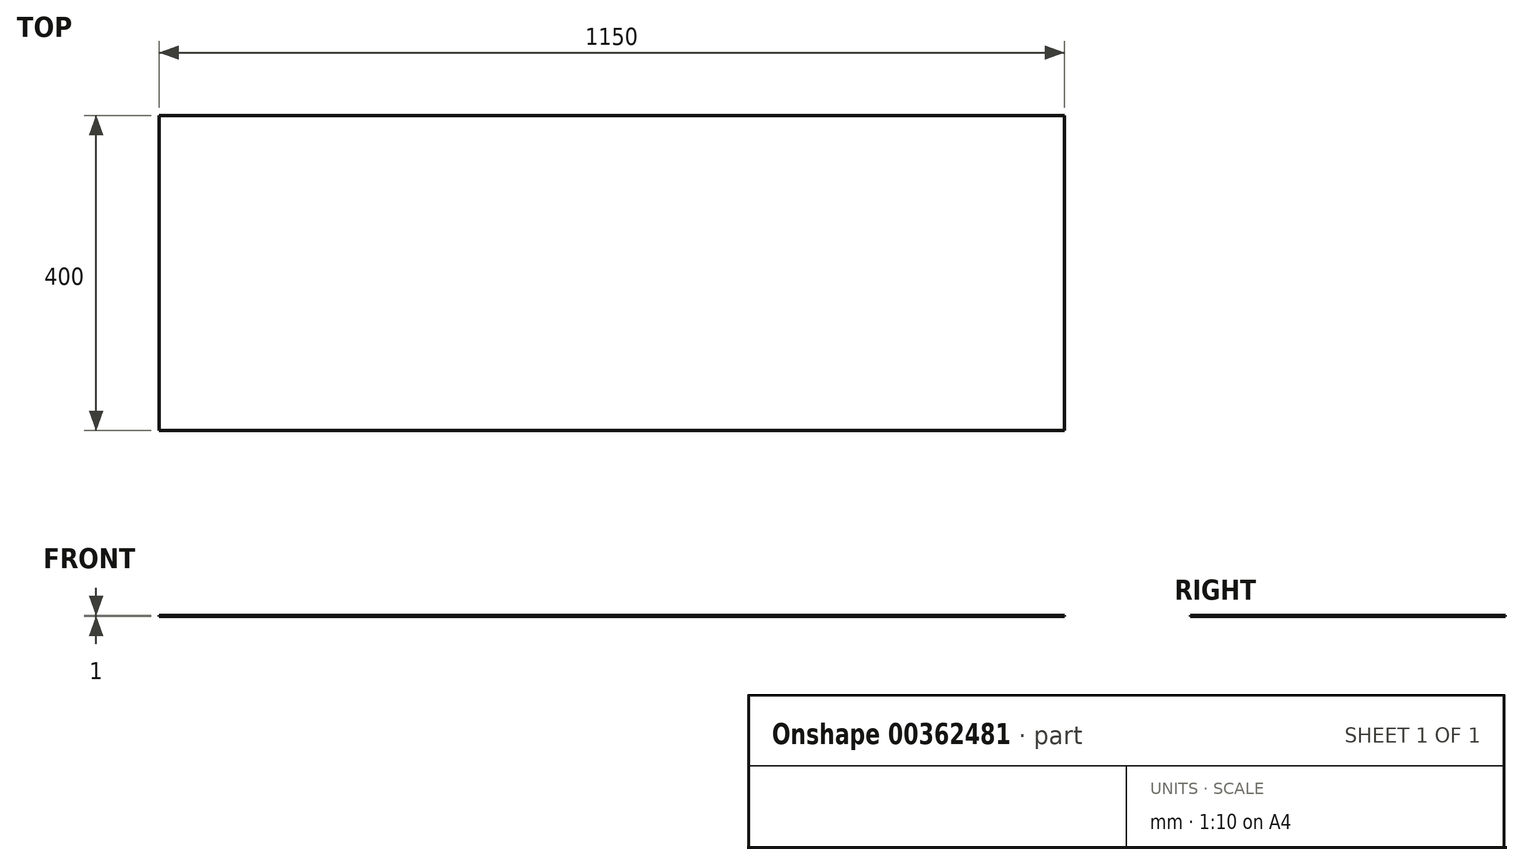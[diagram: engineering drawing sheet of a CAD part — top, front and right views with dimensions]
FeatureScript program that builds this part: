
annotation { "Feature Type Name" : "Feature", "Feature Type Description" : "" }
export const myFeature = defineFeature(function(context is Context, id is Id, definition is map)
    precondition{}
    {
        {
            var Q0;
            Q0=qCreatedBy(makeId("Top.planeOp"),FACE);
            var sketch = newSketch(context, id + "F0", { "sketchPlane" : qUnion([Q0])});
            skLineSegment(sketch, "E0.bottom", {"start": v(575, 200) * mm, "end": v(-575, 200) * mm});
            skLineSegment(sketch, "E0.top", {"start": v(575, -200) * mm, "end": v(-575, -200) * mm});
            skLineSegment(sketch, "E0.left", {"start": v(575, 200) * mm, "end": v(575, -200) * mm});
            skLineSegment(sketch, "E0.right", {"start": v(-575, 200) * mm, "end": v(-575, -200) * mm});
            skPoint(sketch, "E0.middle", {"position": v(0, 0) * mm});
            skSolve(sketch);
        }
        {
            var Q0;
            Q0 = qSketchRegion(id + "F0", true);
            extrude(context, id + "F1", {"entities" : qUnion([Q0]), "depth" : 1 * mm});
        }
        {
            var Q0;
            Q0=qCreatedBy(makeId("Front.planeOp"),FACE);
            var sketch = newSketch(context, id + "F2", { "sketchPlane" : qUnion([Q0])});
            skLineSegment(sketch, "E1", {"start": v(-575, 261) * mm, "end": v(575, 261) * mm});
            skSolve(sketch);
        }
    });
